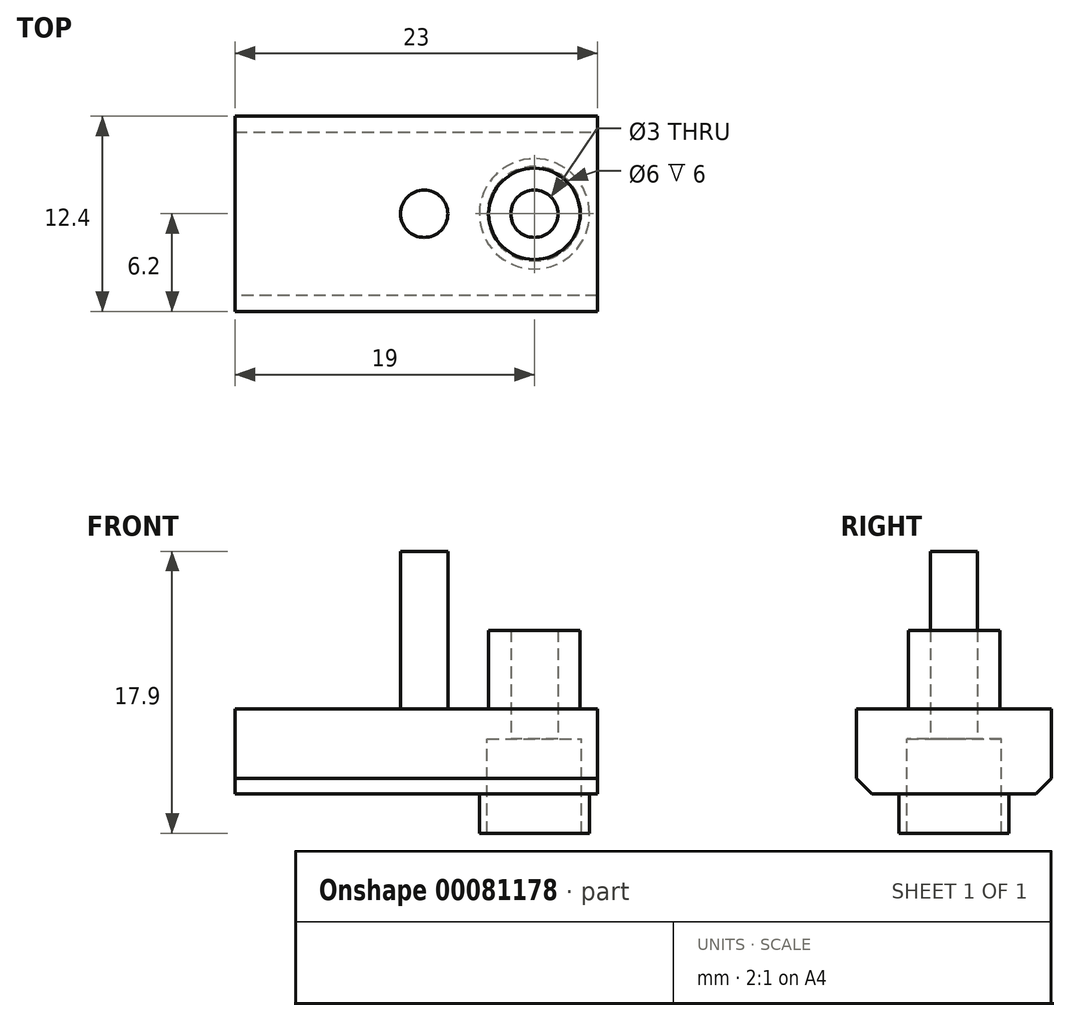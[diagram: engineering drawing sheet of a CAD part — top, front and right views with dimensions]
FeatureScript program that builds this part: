
annotation { "Feature Type Name" : "Feature", "Feature Type Description" : "" }
export const myFeature = defineFeature(function(context is Context, id is Id, definition is map)
    precondition{}
    {
        {
            var Q0;
            Q0=qCreatedBy(makeId("Top.planeOp"),FACE);
            var sketch = newSketch(context, id + "F0", { "sketchPlane" : qUnion([Q0])});
            skLineSegment(sketch, "E0.bottom", {"start": v(0, 0) * mm, "end": v(23, 0) * mm});
            skLineSegment(sketch, "E0.top", {"start": v(0, 12.4) * mm, "end": v(23, 12.4) * mm});
            skLineSegment(sketch, "E0.left", {"start": v(0, 0) * mm, "end": v(0, 12.4) * mm});
            skLineSegment(sketch, "E0.right", {"start": v(23, 0) * mm, "end": v(23, 12.4) * mm});
            skCircle(sketch, "E1", {"center": v(19, 6.2) * mm, "radius": 1.5 * mm});
            skLineSegment(sketch, "E2", {"start": v(19, 6.2) * mm, "end": v(23, 6.2) * mm, "construction": true});
            skSolve(sketch);
        }
        {
            var Q0;
            Q0=qSketchRegion(id+"F0",true);
            extrude(context, id + "F1", {"entities" : qUnion([Q0]), "depth" : 5.4 * mm});
        }
        {
            var Q0;
            Q0=makeQuery(id+"F1.opExtrude","CAP_EDGE",EDGE,{"disambiguationData":[OSD([sQuery(id+"F0.wireOp",EDGE,"E0.bottom")])],"isStart":true});
            var Q1;
            Q1=makeQuery(id+"F1.opExtrude","CAP_EDGE",EDGE,{"disambiguationData":[OSD([sQuery(id+"F0.wireOp",EDGE,"E0.top")])],"isStart":true});
            chamfer(context, id + "F2", {"entities" : qUnion([Q0, Q1]), "width" : 1 * mm, "tangentPropagation" : true});
        }
        {
            var Q0;
            Q0=makeQuery(id+"F1.opExtrude","CAP_FACE",FACE,{"disambiguationData":[OSD([sQuery(id+"F0.wireOp",EDGE,"E0.bottom"),sQuery(id+"F0.wireOp",EDGE,"E0.top"),sQuery(id+"F0.wireOp",EDGE,"E0.left"),sQuery(id+"F0.wireOp",EDGE,"E0.right"),sQuery(id+"F0.wireOp",EDGE,"E1")])],"isStart":false});
            var sketch = newSketch(context, id + "F3", { "sketchPlane" : qUnion([Q0])});
            skCircle(sketch, "E3", {"center": v(19, 6.2) * mm, "radius": 2.9 * mm});
            skSolve(sketch);
        }
        {
            var Q0;
            Q0=makeQuery(id+"F3.imprint","IMPRINT",FACE,{"disambiguationData":[TD([[makeQuery(id+"F3.imprint","IMPRINT",EDGE,{"derivedFrom":sQuery(id+"F3.wireOp",EDGE,"E3")}),1.0]])]});
            extrude(context, id + "F4", {"entities" : qUnion([Q0]), "operationType" : NewBodyOperationType.ADD, "depth" : 5 * mm});
        }
        {
            var Q0;
            Q0=makeQuery(id+"F1.opExtrude","CAP_FACE",FACE,{"disambiguationData":[OSD([sQuery(id+"F0.wireOp",EDGE,"E0.bottom"),sQuery(id+"F0.wireOp",EDGE,"E0.top"),sQuery(id+"F0.wireOp",EDGE,"E0.left"),sQuery(id+"F0.wireOp",EDGE,"E0.right"),sQuery(id+"F0.wireOp",EDGE,"E1")])],"isStart":true});
            var sketch = newSketch(context, id + "F5", { "sketchPlane" : qUnion([Q0])});
            skCircle(sketch, "E4", {"center": v(19, -6.2) * mm, "radius": 3.5 * mm});
            skCircle(sketch, "E5", {"center": v(19, -6.2) * mm, "radius": 3 * mm});
            skSolve(sketch);
        }
        {
            var Q0;
            Q0=makeQuery(id+"F5.imprint","IMPRINT",FACE,{"disambiguationData":[TD([[makeQuery(id+"F5.imprint","IMPRINT",EDGE,{"derivedFrom":sQuery(id+"F5.wireOp",EDGE,"E4")}),1.0]])]});
            extrude(context, id + "F6", {"entities" : qUnion([Q0]), "operationType" : NewBodyOperationType.ADD, "depth" : 2.5 * mm});
        }
        {
            var Q0;
            {var subQ0=sQuery(id+"F0.wireOp",EDGE,"E1");Q0=makeQuery(id+"F6.boolean.opBoolean","SPLIT",FACE,{"disambiguationData":[TD([makeQuery(id+"F1.opExtrude","SWEPT_FACE",FACE,{"disambiguationData":[OSD([subQ0])]})])],"derivedFrom":makeQuery(id+"F1.opExtrude","CAP_FACE",FACE,{"disambiguationData":[OSD([sQuery(id+"F0.wireOp",EDGE,"E0.bottom"),sQuery(id+"F0.wireOp",EDGE,"E0.top"),sQuery(id+"F0.wireOp",EDGE,"E0.left"),sQuery(id+"F0.wireOp",EDGE,"E0.right"),subQ0])],"isStart":true})});}
            extrude(context, id + "F7", {"entities" : qUnion([Q0]), "operationType" : NewBodyOperationType.REMOVE, "oppositeDirection" : true, "depth" : 3.5 * mm});
        }
        {
            var Q0;
            Q0=makeQuery(id+"F1.opExtrude","CAP_FACE",FACE,{"disambiguationData":[OSD([sQuery(id+"F0.wireOp",EDGE,"E0.bottom"),sQuery(id+"F0.wireOp",EDGE,"E0.top"),sQuery(id+"F0.wireOp",EDGE,"E0.left"),sQuery(id+"F0.wireOp",EDGE,"E0.right"),sQuery(id+"F0.wireOp",EDGE,"E1")])],"isStart":false});
            var sketch = newSketch(context, id + "F8", { "sketchPlane" : qUnion([Q0])});
            skCircle(sketch, "E6", {"center": v(12, 6.2) * mm, "radius": 1.5 * mm});
            skLineSegment(sketch, "E7", {"start": v(12, 6.2) * mm, "end": v(0, 6.2) * mm, "construction": true});
            skSolve(sketch);
        }
        {
            var Q0;
            Q0=qSketchRegion(id+"F8",true);
            extrude(context, id + "F9", {"entities" : qUnion([Q0]), "operationType" : NewBodyOperationType.ADD, "depth" : 10 * mm});
        }
    });
